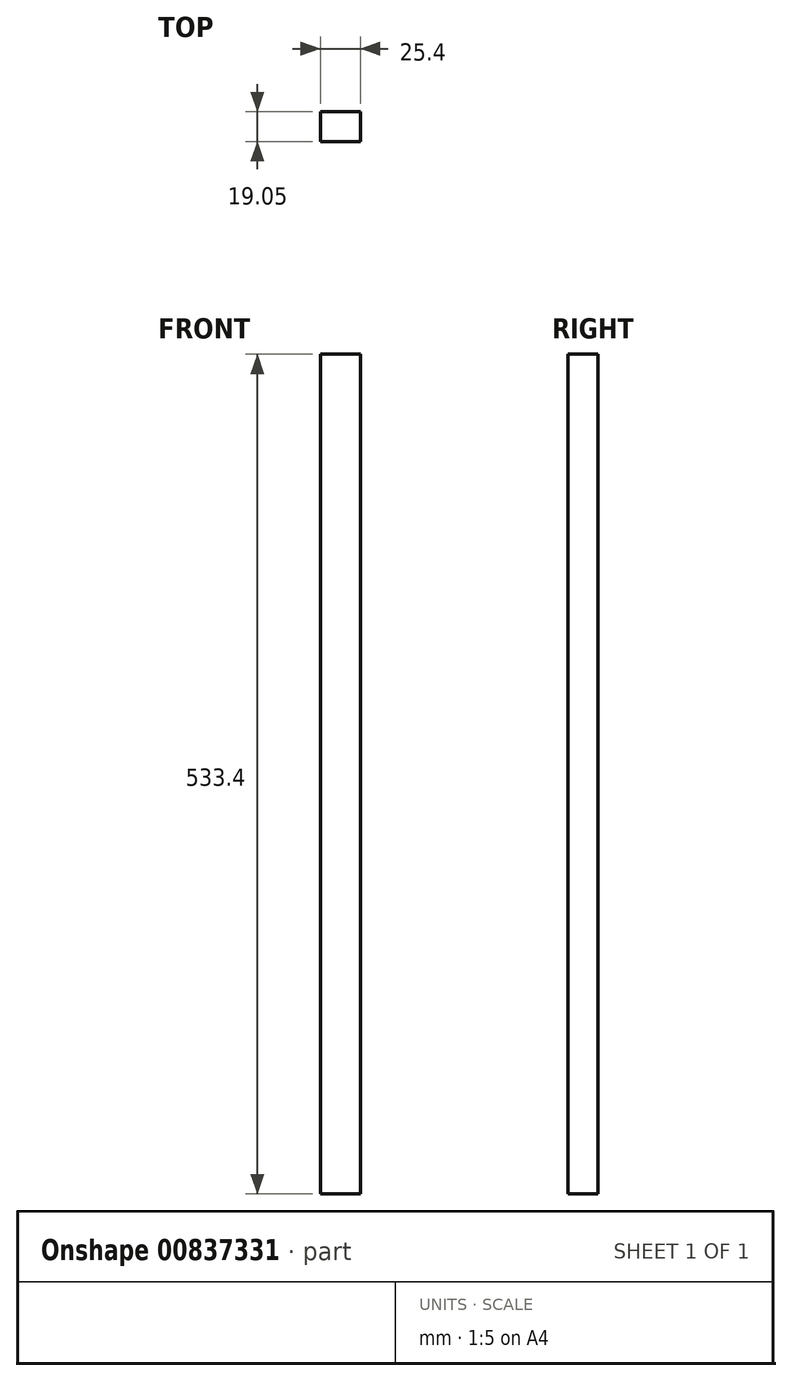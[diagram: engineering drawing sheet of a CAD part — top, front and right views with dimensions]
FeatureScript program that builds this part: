
annotation { "Feature Type Name" : "Feature", "Feature Type Description" : "" }
export const myFeature = defineFeature(function(context is Context, id is Id, definition is map)
    precondition{}
    {
        {
            var Q0;
            Q0=qCreatedBy(makeId("Front.planeOp"),FACE);
            var sketch = newSketch(context, id + "F0", { "sketchPlane" : qUnion([Q0])});
            skLineSegment(sketch, "E0.bottom", {"start": v(0, 0) * mm, "end": v(25.4, 0) * mm});
            skLineSegment(sketch, "E0.top", {"start": v(0, 533.4) * mm, "end": v(25.4, 533.4) * mm});
            skLineSegment(sketch, "E0.left", {"start": v(0, 0) * mm, "end": v(0, 533.4) * mm});
            skLineSegment(sketch, "E0.right", {"start": v(25.4, 0) * mm, "end": v(25.4, 533.4) * mm});
            skSolve(sketch);
        }
        {
            var Q0;
            Q0=makeQuery(id+"F0.imprint","IMPRINT",FACE,{"disambiguationData":[TD([[makeQuery(id+"F0.imprint","IMPRINT",EDGE,{"derivedFrom":sQuery(id+"F0.wireOp",EDGE,"E0.bottom")}),1.0]])]});
            extrude(context, id + "F1", {"entities" : qUnion([Q0]), "depth" : 19.05 * mm, "offsetDistance" : 25.4 * mm});
        }
    });
